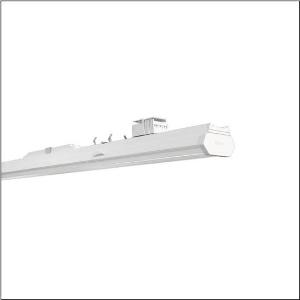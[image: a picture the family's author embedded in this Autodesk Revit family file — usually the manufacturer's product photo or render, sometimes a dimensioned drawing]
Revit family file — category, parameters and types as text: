
# Revit family: licross_11_protected_mo_51td1bcn68xg
name_source: partatom
category: Lighting Fixtures
units: mm (PartAtom-declared; Revit-internal decimal feet)

## family parameters
Cut with Voids When Loaded = No
Host = Face
Light Source = No
Part Type = Normal
Room Calculation Point = No
Round Connector Dimension = Use Diameter
Shared = No

## types (1)
- --- (1 x LED, 8310 lm, 49.4 W, 6500K)
    Apparent Load = 49 VA
    CIE Flux Codes = 54 82 95 97 100
    Color Rendering = 80
    Color Temperature = 6500K
    Default Elevation = 1800 mm
    Description = Licross 11 Protected MO, luminaire insert, of sheet steel, galvanised, coil coated, white, length: 1.500mm, width: 90mm, height: 101mm, LED rated luminous flux: 8.310lm, light colour: 865, SDCM (Standard Deviation of Colour Matching)MacAdam ≤ 2 SDCM (initial), control gear: ON/OFF Multilumen, CLOi, with plug, 3-pole, with phase selection, mains connection: 220..240V, AC, 50/60Hz, start of lifetime: 49W, end of service life: 55W, internal wiring halogen-free, primary optical cover: cover, of PMMA, light emission: direct distribution, primary light characteristic: symmetric, protection rating (complete): IP54, insulation class (complete): insulation class I (protective earthing), certification: CE, ENEC, VDE, UKCA, protection symbol: D if used in an environment with non-conductive dust loads with corresponding accessories, impact resistance: IK06, permissible ambient temperature for indoor applications: -35..+40°C, corresponds to IFS (International Featured Standards) requirements for safety and quality in the food industry, reducing of maximum allowable ambient temperature of 5°C with ceiling mounting, LABS conformity tested according to VDMA 24364:2018-05, The light source and the operating device comply with the requirements of the Ecodesign Regulation (EU) 2019/2020 and are replaceable in accordance with this regulation, packaging unit: 1 piece
    Height = 92 mm
    Lamp = 1 x LED
    Lamp Light Flux = 8310 lm
    Lamp Power = 49.4 W
    Lamp count = 1
    Length = 1500 mm
    Luminous efficacy = 168 lm/W
    Manufacturer = Siteco
    ModVariant = No
    Model = 51TD1BCN68XG
    Mounting Place = Ceiling
    Mounting Type = Pendant
    Number of Poles = 1
    OnlyDefault = Yes
    Power Factor = 1
    Product Name = Licross 11 Protected MO
    Product group = luminaire insert | ceiling pendant
    ProductGroupID = 901
    Protection Class = Protection class I
    Protection Degree = IP 54
    RLX_Detail_Level = 1
    RLX_Emergency_Light_Flux = 0 lm
    RLX_Emergency_Type = 0
    RLX_Emergency_Type_DB = No
    RlxData = <blob elided: 22325 chars, md5=9de1bb57>
    Socket = socket
    Standby Power = 0 W
    System Light Flux = 8310 lm
    System Power = 49 W
    Type Comments = factory setting: luminous flux: 100 % | (A | C | E) | 113 mA
    Type Image = l_1256145.jpg
    URL = http://relux.com
    VarID = @adj_000951
    Voltage = 0 V
    Weight = 0.00 kg
    Width = 88 mm

## geometry (parser evidence)
native form markers: Blend x4, Sweep x10
no freeform markers — native parametric forms only
